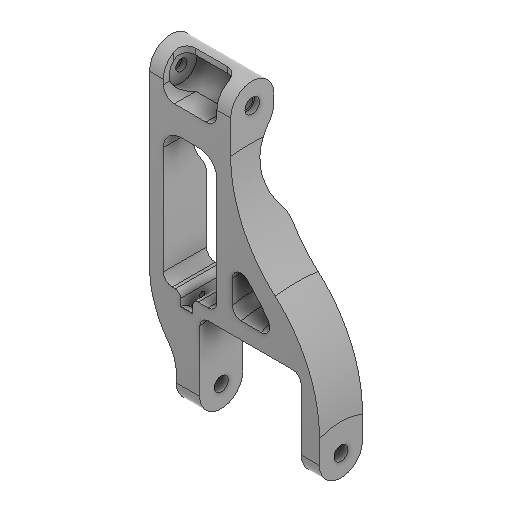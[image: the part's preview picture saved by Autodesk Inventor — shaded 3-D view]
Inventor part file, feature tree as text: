
AUTODESK INVENTOR PART (.ipt)
format: ipt  version: 2025 (Build 290162000, 162)  size: 608,768 bytes
history: native  units: in
note: dims shown in document units (in); Inventor stores cm internally (conversion verified against a paired STEP export)
features: extrude x23, sketch x23, projected_geometry x20, fillet x12, plane x4, other x3, mirror x2, reference x1
ambient origin geometry x8: Origin, YZ Plane, XZ Plane, XY Plane, X Axis, Y Axis, Z Axis, Center Point
bodies: Solid1 (feature_tree)
feature tree (88):
  extrude  "Extrusion1"  Depth=0.315in TaperAngle=0.0deg
  extrude  "Extrusion2"  Depth=0.2559in
  extrude  "Extrusion3"  Depth=0.1181in
  plane  "Work Plane1"
  mirror  "Mirror1"
  extrude  "Extrusion4"  Depth=0.315in TaperAngle=0.0deg
  extrude  "Extrusion5"  Depth=0.5in
  fillet  "Fillet1"  Radius=1.0in
  extrude  "Extrusion6"  Depth=0.25in
  fillet  "Fillet2"  [1 undecoded]
  fillet  "Fillet4"  Radius=0.3228in
  plane  "Work Plane2"
  extrude  "Extrusion7"  Depth=0.75in
  fillet  "Fillet5"  Radius=0.2362in
  extrude  "Extrusion8"  Depth=0.3937in
  fillet  "Fillet6"  Radius=0.3937in
  extrude  "Extrusion9"  [1 undecoded]
  mirror  "Mirror2"
  fillet  "Fillet7"  Radius=1.5507in
  plane  "Work Plane3"
  sketch  "Sketch11"  dims[d38=0.4724in d39=0.0in d40=3.0in]
  plane  "Work Plane4"
  extrude  "Extrusion11"  Depth=3.0in
  extrude  "Extrusion12"  Depth=0.25in
  fillet  "Fillet8"  Radius=0.25in
  extrude  "Extrusion14"  Depth=0.25in TaperAngle=0.0deg
  fillet  "Fillet9"  [1 undecoded]
  fillet  "Fillet12"  Radius=3.324in
  fillet  "Fillet13"  [1 undecoded]
  extrude  "Extrusion15"  Depth=0.1575in TaperAngle=0.0deg
  extrude  "Extrusion16"  Depth=0.3937in TaperAngle=0.0deg
  extrude  "Extrusion18"  Depth=1.1811in TaperAngle=0.0deg
  extrude  "Extrusion17"  TaperAngle=0.0deg  [1 undecoded]
  extrude  "Extrusion19"  Depth=0.5118in
  extrude  "Extrusion20"  TaperAngle=0.0deg  [1 undecoded]
  extrude  "Extrusion21"  TaperAngle=0.0deg  [1 undecoded]
  fillet  "Fillet14"  [1 undecoded]
  extrude  "Extrusion22"  [1 undecoded]
  fillet  "Fillet15"  [1 undecoded]
  extrude  "Extrusion23"  [1 undecoded]
  extrude  "Extrusion24"  [1 undecoded]
  extrude  "Extrusion25"  [1 undecoded]
  sketch  "Sketch1"  dims[d0=0.3346in d1=0.315in d2=0.0in]
  sketch  "Sketch2"  dims[d3=0.0787in d4=0.0in d5=0.2559in]
  projected_geometry  "Projected Loop1"
  sketch  "Sketch3"  dims[d6=0.1181in d7=0.0in d8=0.1181in]
  projected_geometry  "Projected Loop2"
  sketch  "Sketch4"  dims[d9=0.6102in d10=0.315in d11=0.0in]
  projected_geometry  "Projected Loop3"
  sketch  "Sketch5"  dims[d12=0.0in d13=0.0in d14=0.5in d15=1.0in d16=0.0in]
  projected_geometry  "Projected Loop4"
  sketch  "Sketch6"  dims[d17=0.25in d19=0.4in d20=-1.0836in d21=0.3228in]
  projected_geometry  "Projected Loop5"
  sketch  "Sketch7"  dims[d22=0.4724in d23=0.0in d24=0.75in d25=0.2362in]
  projected_geometry  "Projected Loop6"
  reference  "Reference1"
  sketch  "Sketch8"  dims[d26=0.1575in d27=0.0in d28=2.0in d29=0.3937in d30=0.0in]
  sketch  "Sketch9"  dims[d31=0.25in d33=-0.2362in d36=1.5507in d37=0.0in]
  projected_geometry  "Projected Loop7"
  projected_geometry  "Projected Loop9"
  sketch  "Sketch12"  dims[d43=0.0in d44=0.0in d45=0.1969in d49=0.25in]
  projected_geometry  "Projected Loop10"
  projected_geometry  "Projected Loop11"
  sketch  "Sketch14"  dims[d50=0.25in d51=0.0591in d52=0.0in d53=0.0in d54=0.0in d55=3.324in d56=0.0in d57=0.0in]
  projected_geometry  "Projected Loop12"
  sketch  "Sketch15"  dims[d58=1.0in d59=0.0in d60=0.1575in d61=0.0in]
  projected_geometry  "Projected Loop13"
  sketch  "Sketch16"  dims[d62=0.3937in d63=0.0in d64=1.0in d65=0.0in]
  projected_geometry  "Projected Loop14"
  sketch  "Sketch17"  dims[d66=0.2in d67=1.1811in d68=0.0in]
  sketch  "Sketch18"  dims[d69=0.125in d70=0.0in d71=0.0in]
  sketch  "Sketch19"  dims[d72=1.0in d73=0.0in d74=0.5118in]
  projected_geometry  "Projected Loop15"
  projected_geometry  "Projected Loop16"
  projected_geometry  "Projected Loop17"
  sketch  "Sketch21"  dims[d75=0.5in d76=0.0in d48=0.0in]
  projected_geometry  "Projected Loop19"
  sketch  "Sketch22"  dims[d78=0.0in d79=0.0in d80=0.0in]
  projected_geometry  "Projected Loop20"
  sketch  "Sketch23"  dims[d77=0.0in]
  sketch  "Sketch24"
  projected_geometry  "Projected Loop21"
  sketch  "Sketch25"
  projected_geometry  "Projected Loop22"
  sketch  "Sketch26"
  other  "<userpath>\Desktop\puppycat\woodhouseMK1.iam"
  other  "woodhouseMK1.iam"
  other  "6082rsBearing:25"
note: 13 required parameter values undecoded (feature->parameter linkage not recoverable at this tier; creation-order binding heuristic only, values carry confidence <= 0.55)
